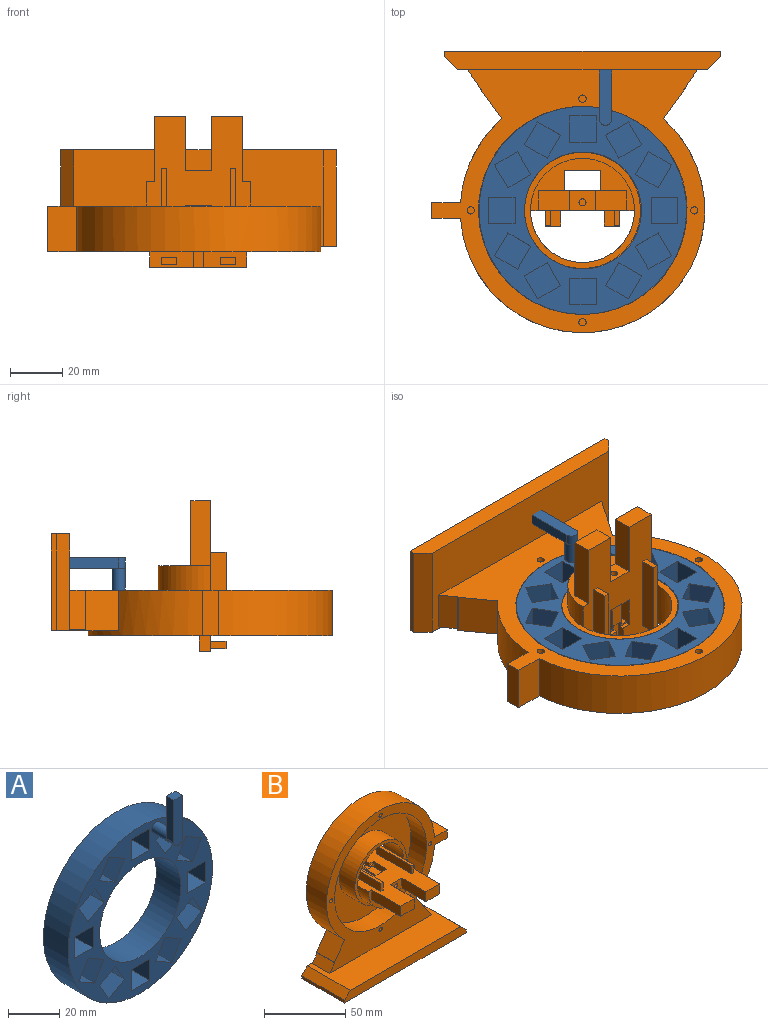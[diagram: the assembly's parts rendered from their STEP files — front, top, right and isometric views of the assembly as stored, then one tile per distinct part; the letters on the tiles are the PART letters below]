
ASSEMBLY  parts=2 mates=1
PART A: 72 faces, bbox 80x26x95.6 mm
  f0: plane 4.95x2.84mm, normal (0,-1,0), area 0.2mm2, adj f65,f67,f68,f70
  f1: plane 10.6x8.83mm, normal (-0.87,0,0.5), area 108.1mm2, adj f2,f38,f51,f64
  f2: plane 10.6x8.83mm, normal (0.5,0,0.87), area 108.1mm2, adj f1,f3,f51,f64
  f3: plane 10.6x8.83mm, normal (0.87,0,-0.5), area 108.1mm2, adj f2,f38,f51,f64
  f4: plane 10.6x8.83mm, normal (-0.87,0,-0.5), area 108.1mm2, adj f5,f39,f51,f63
  f5: plane 10.6x8.83mm, normal (-0.5,0,0.87), area 108.1mm2, adj f4,f6,f51,f63
  f6: plane 10.6x8.83mm, normal (0.87,0,0.5), area 108.1mm2, adj f5,f39,f51,f63
  f7: plane 10.6x10.2mm, normal (0,0,-1), area 108.1mm2, adj f8,f40,f51,f62
  f8: plane 10.6x10.2mm, normal (-1,0,0), area 108.1mm2, adj f7,f9,f51,f62
  f9: plane 10.6x10.2mm, normal (0,0,1), area 108.1mm2, adj f8,f40,f51,f62
  f10: plane 10.6x8.83mm, normal (0.87,0,-0.5), area 108.1mm2, adj f11,f41,f51,f61
  f11: plane 10.6x8.83mm, normal (-0.5,0,-0.87), area 108.1mm2, adj f10,f12,f51,f61
  f12: plane 10.6x8.83mm, normal (-0.87,0,0.5), area 108.1mm2, adj f11,f41,f51,f61
  f13: plane 10.6x8.83mm, normal (0.5,0,-0.87), area 108.1mm2, adj f14,f42,f51,f60
  f14: plane 10.6x8.83mm, normal (-0.87,0,-0.5), area 108.1mm2, adj f13,f15,f51,f60
  f15: plane 10.6x8.83mm, normal (-0.5,0,0.87), area 108.1mm2, adj f14,f42,f51,f60
  f16: plane 10.6x10.2mm, normal (1,0,0), area 108.1mm2, adj f17,f43,f51,f59
  f17: plane 10.6x10.2mm, normal (0,0,-1), area 108.1mm2, adj f16,f18,f51,f59
  f18: plane 10.6x10.2mm, normal (-1,0,0), area 108.1mm2, adj f17,f43,f51,f59
  f19: plane 10.6x8.83mm, normal (0.5,0,0.87), area 108.1mm2, adj f20,f44,f51,f58
  f20: plane 10.6x8.83mm, normal (0.87,0,-0.5), area 108.1mm2, adj f19,f21,f51,f58
  f21: plane 10.6x8.83mm, normal (-0.5,0,-0.87), area 108.1mm2, adj f20,f44,f51,f58
  f22: plane 10.6x8.83mm, normal (0.87,0,0.5), area 108.1mm2, adj f23,f45,f51,f57
  f23: plane 10.6x8.83mm, normal (0.5,0,-0.87), area 108.1mm2, adj f22,f24,f51,f57
  f24: plane 10.6x8.83mm, normal (-0.87,0,-0.5), area 108.1mm2, adj f23,f45,f51,f57
  f25: plane 10.6x10.2mm, normal (0,0,1), area 108.1mm2, adj f26,f46,f51,f56
  f26: plane 10.6x10.2mm, normal (1,0,0), area 108.1mm2, adj f25,f27,f51,f56
  f27: plane 10.6x10.2mm, normal (0,0,-1), area 108.1mm2, adj f26,f46,f51,f56
  f28: plane 10.6x8.83mm, normal (-0.87,0,0.5), area 108.1mm2, adj f29,f47,f51,f55
  f29: plane 10.6x8.83mm, normal (0.5,0,0.87), area 108.1mm2, adj f28,f30,f51,f55
  f30: plane 10.6x8.83mm, normal (0.87,0,-0.5), area 108.1mm2, adj f29,f47,f51,f55
  f31: plane 10.6x8.83mm, normal (-0.5,0,0.87), area 108.1mm2, adj f32,f48,f51,f54
  f32: plane 10.6x8.83mm, normal (0.87,0,0.5), area 108.1mm2, adj f31,f33,f51,f54
  f33: plane 10.6x8.83mm, normal (0.5,0,-0.87), area 108.1mm2, adj f32,f48,f51,f54
  f34: plane 10.6x10.2mm, normal (-1,0,0), area 108.1mm2, adj f35,f49,f51,f53
  f35: plane 10.6x10.2mm, normal (0,0,1), area 108.1mm2, adj f34,f36,f51,f53
  f36: plane 10.6x10.2mm, normal (1,0,0), area 108.1mm2, adj f35,f49,f51,f53
  f37: cylinder r=40mm len=80mm, axis (0,1,0), area 3418.1mm2, adj f51,f52
  f38: plane 10.6x8.83mm, normal (-0.5,0,-0.87), area 108.1mm2, adj f1,f3,f51,f64
  f39: plane 10.6x8.83mm, normal (0.5,0,-0.87), area 108.1mm2, adj f4,f6,f51,f63
  f40: plane 10.6x10.2mm, normal (1,0,0), area 108.1mm2, adj f7,f9,f51,f62
  f41: plane 10.6x8.83mm, normal (0.5,0,0.87), area 108.1mm2, adj f10,f12,f51,f61
  f42: plane 10.6x8.83mm, normal (0.87,0,0.5), area 108.1mm2, adj f13,f15,f51,f60
  f43: plane 10.6x10.2mm, normal (0,0,1), area 108.1mm2, adj f16,f18,f51,f59
  f44: plane 10.6x8.83mm, normal (-0.87,0,0.5), area 108.1mm2, adj f19,f21,f51,f58
  f45: plane 10.6x8.83mm, normal (-0.5,0,0.87), area 108.1mm2, adj f22,f24,f51,f57
  f46: plane 10.6x10.2mm, normal (-1,0,0), area 108.1mm2, adj f25,f27,f51,f56
  f47: plane 10.6x8.83mm, normal (-0.5,0,-0.87), area 108.1mm2, adj f28,f30,f51,f55
  f48: plane 10.6x8.83mm, normal (-0.87,0,-0.5), area 108.1mm2, adj f31,f33,f51,f54
  f49: plane 10.6x10.2mm, normal (0,0,-1), area 108.1mm2, adj f34,f36,f51,f53
  f50: cylinder r=22.5mm len=45mm, axis (0,1,0), area 1922.7mm2, adj f51,f52
  f51: plane 80x80mm, normal (0,-1,0), area 2168.4mm2, adj f1,f2,f3,f4,f5,f6,f7,f8
  f52: plane 80x80mm, normal (0,1,0), area 3436.1mm2, adj f37,f50
  f53: plane 10.2x10.2mm, normal (0,-1,0), area 104mm2, adj f34,f35,f36,f49
  f54: plane 13.93x13.93mm, normal (0,-1,0), area 104mm2, adj f31,f32,f33,f48
  f55: plane 13.93x13.93mm, normal (0,-1,0), area 104mm2, adj f28,f29,f30,f47
  f56: plane 10.2x10.2mm, normal (0,-1,0), area 104mm2, adj f25,f26,f27,f46
  f57: plane 13.93x13.93mm, normal (0,-1,0), area 104mm2, adj f22,f23,f24,f45
  f58: plane 13.93x13.93mm, normal (0,-1,0), area 104mm2, adj f19,f20,f21,f44
  f59: plane 10.2x10.2mm, normal (0,-1,0), area 104mm2, adj f16,f17,f18,f43
  f60: plane 13.93x13.93mm, normal (0,-1,0), area 104mm2, adj f13,f14,f15,f42
  f61: plane 13.93x13.93mm, normal (0,-1,0), area 104mm2, adj f10,f11,f12,f41
  f62: plane 10.2x10.2mm, normal (0,-1,0), area 104mm2, adj f7,f8,f9,f40
  f63: plane 13.93x13.93mm, normal (0,-1,0), area 104mm2, adj f4,f5,f6,f39
  f64: plane 13.93x13.93mm, normal (0,-1,0), area 104mm2, adj f1,f2,f3,f38
  f65: cylinder r=2.48mm len=8.3mm, axis (0,1,0), area 129.2mm2, adj f0,f51,f66
  f66: plane 19.94x4.9mm, normal (0,1,0), area 89.9mm2, adj f65,f68,f69,f70
  f67: cylinder r=2.45mm len=4.9mm, axis (0,1,0), area 31.6mm2, adj f0,f68,f70,f71
  f68: plane 20.3x4.1mm, normal (1,0,0), area 83.2mm2, adj f0,f66,f67,f69,f71
  f69: plane 4.9x4.1mm, normal (0,0,1), area 20.1mm2, adj f66,f68,f70,f71
  f70: plane 20.3x4.1mm, normal (-1,0,0), area 83.2mm2, adj f0,f66,f67,f69,f71
  f71: plane 22.75x4.9mm, normal (0,-1,0), area 108.9mm2, adj f67,f68,f69,f70
PART B: 124 faces, bbox 111x58x108.1 mm
  f0: plane 58x40mm, normal (0,0,1), area 1621.6mm2, adj f1,f2,f3,f4,f7,f8,f9,f19
  f1: plane 3.38x1.5mm, normal (0,-1,0), area 5.1mm2, adj f0,f9,f16,f101
  f2: plane 6x2mm, normal (0,1,0), area 12mm2, adj f0,f19,f46,f47
  f3: plane 6x2mm, normal (0,1,0), area 12mm2, adj f0,f43,f44,f45
  f4: plane 40x20mm, normal (0,1,0), area 303.4mm2, adj f0,f5,f17,f23,f24,f41,f42,f60
  f5: plane 19.01x5.3mm, normal (0,0,-1), area 52.7mm2, adj f4,f6,f20,f21,f22,f23,f40,f42
  f6: plane 4.7x1.3mm, normal (0,1,0), area 6.1mm2, adj f5,f20,f42,f61
  f7: plane 40x20mm, normal (0,-1,0), area 260.7mm2, adj f0,f41,f42,f49,f50,f51,f52,f92
  f8: plane 11.65x5.53mm, normal (1,0,0), area 57.8mm2, adj f0,f13,f14,f16,f90,f91,f93
  f9: plane 11.65x5.53mm, normal (-1,0,0), area 57.8mm2, adj f0,f1,f10,f12,f16,f91,f93
  f10: plane 4.03x2.5mm, normal (0,-1,0), area 10.1mm2, adj f9,f11,f16,f93
  f11: plane 10.03x4.03mm, normal (1,0,0), area 40.4mm2, adj f10,f12,f16,f93
  f12: plane 4.03x2.5mm, normal (0,1,0), area 10.1mm2, adj f9,f11,f16,f93
  f13: plane 4.03x2.5mm, normal (0,-1,0), area 10.1mm2, adj f8,f15,f16,f93
  f14: plane 4.03x2.5mm, normal (0,1,0), area 10.1mm2, adj f8,f15,f16,f93
  f15: plane 10.03x4.03mm, normal (-1,0,0), area 40.4mm2, adj f13,f14,f16,f93
  f16: plane 11.65x10.25mm, normal (0,0,1), area 62.3mm2, adj f1,f8,f9,f10,f11,f12,f13,f14
  f17: plane 19.01x5.22mm, normal (0,0,-1), area 51.2mm2, adj f4,f18,f24,f25,f26,f27,f28,f92
  f18: plane 7x4.7mm, normal (1,0,0), area 32.9mm2, adj f17,f25,f26,f60
  f19: plane 30.2x6mm, normal (-1,0,0), area 181.2mm2, adj f0,f2,f47,f59
  f20: plane 5.01x4.7mm, normal (-1,0,0), area 23.5mm2, adj f5,f6,f21,f61
  f21: plane 4.7x4mm, normal (0,1,0), area 18.8mm2, adj f5,f20,f40,f61
  f22: plane 4.7x4mm, normal (0,-1,0), area 18.8mm2, adj f5,f23,f40,f61
  f23: plane 7x4.7mm, normal (-1,0,0), area 32.9mm2, adj f4,f5,f22,f61
  f24: plane 7x4.7mm, normal (1,0,0), area 32.9mm2, adj f4,f17,f25,f60
  f25: plane 4.7x4mm, normal (0,-1,0), area 18.8mm2, adj f17,f18,f24,f60
  f26: plane 4.7x4mm, normal (0,1,0), area 18.8mm2, adj f17,f18,f27,f60
  f27: plane 5.01x4.7mm, normal (1,0,0), area 23.5mm2, adj f17,f26,f28,f60
  f28: plane 4.7x1.22mm, normal (0,1,0), area 5.7mm2, adj f17,f27,f60,f92
  f29: plane 106x37.2mm, normal (0,0,-1), area 3778.4mm2, adj f31,f73,f74,f77,f79,f80,f81
  f30: plane 105x101.14mm, normal (0,-1,0), area 2880mm2, adj f32,f33,f36,f37,f68,f69,f70,f71
  f31: plane 106x25.92mm, normal (0,1,0), area 1453.7mm2, adj f29,f36,f37,f69,f70,f71,f72,f73
  f32: plane 15x6.12mm, normal (-0.82,0,0.57), area 111.8mm2, adj f30,f34,f36,f72
  f33: plane 15x6.12mm, normal (0.82,0,0.57), area 111.8mm2, adj f30,f35,f37,f72
  f34: plane 13.03x6.12mm, normal (0,1,0), area 38.2mm2, adj f32,f36,f72
  f35: plane 13.03x6.12mm, normal (0,1,0), area 38.2mm2, adj f33,f37,f72
  f36: cylinder r=62.5mm len=15.6mm, axis (0,1,0), area 9.5mm2, adj f30,f31,f32,f34,f70,f72
  f37: cylinder r=62.5mm len=15.6mm, axis (0,1,0), area 9.6mm2, adj f30,f31,f33,f35,f69,f72
  f38: plane 80x80mm, normal (0,-1,0), area 3460.8mm2, adj f67,f68
  f39: plane 44.65x44.65mm, normal (0,-1,0), area 309.2mm2, adj f50,f66,f67
  f40: plane 7x4.7mm, normal (-1,0,0), area 32.9mm2, adj f5,f21,f22,f61
  f41: plane 25x14.08mm, normal (0,0,1), area 352mm2, adj f4,f7,f42,f92
  f42: plane 25x9.97mm, normal (-1,0,0), area 160mm2, adj f4,f5,f6,f7,f41,f61,f93,f94
  f43: plane 30.2x6mm, normal (-1,0,0), area 181.2mm2, adj f0,f3,f45,f58
  f44: plane 30.2x6mm, normal (1,0,0), area 181.2mm2, adj f0,f3,f45,f58
  f45: plane 30.2x2mm, normal (0,0,1), area 60.4mm2, adj f3,f43,f44,f58
  f46: plane 30.2x6mm, normal (1,0,0), area 181.2mm2, adj f0,f2,f47,f59
  f47: plane 30.2x2mm, normal (0,0,1), area 60.4mm2, adj f2,f19,f46,f59
  f48: plane 12x7.5mm, normal (0,-1,0), area 90mm2, adj f0,f49,f51,f54
  f49: plane 34x25mm, normal (0,0,-1), area 642mm2, adj f7,f48,f51,f52,f53,f54,f55,f56
  f50: cylinder r=20mm len=40mm, axis (0,1,0), area 590.6mm2, adj f0,f7,f39
  f51: plane 25x7.5mm, normal (-1,0,0), area 187.5mm2, adj f0,f7,f48,f49
  f52: plane 25x7.5mm, normal (1,0,0), area 187.5mm2, adj f0,f7,f49,f53
  f53: plane 12x7.5mm, normal (0,-1,0), area 90mm2, adj f0,f49,f52,f55
  f54: plane 20.8x7.5mm, normal (1,0,0), area 156mm2, adj f0,f48,f49,f56
  f55: plane 20.8x7.5mm, normal (-1,0,0), area 156mm2, adj f0,f49,f53,f56
  f56: plane 10x7.5mm, normal (0,-1,0), area 69.3mm2, adj f0,f49,f54,f55,f57
  f57: cylinder r=1.35mm len=6.19mm, axis (0,1,0), area 52.5mm2, adj f56,f82
  f58: plane 6x2mm, normal (0,-1,0), area 12mm2, adj f0,f43,f44,f45
  f59: plane 6x2mm, normal (0,-1,0), area 12mm2, adj f0,f19,f46,f47
  f60: plane 19.01x5.22mm, normal (0,0,1), area 51.2mm2, adj f4,f18,f24,f25,f26,f27,f28,f92
  f61: plane 19.01x5.3mm, normal (0,0,1), area 52.7mm2, adj f4,f6,f20,f21,f22,f23,f40,f42
  f62: cylinder r=1.4mm len=15.1mm, axis (0,1,0), area 86.4mm2, adj f4,f63,f83,f84,f85
  f63: plane 2.8x2.8mm, normal (0,1,0), area 6.2mm2, adj f62
  f64: cylinder r=1.4mm len=15.1mm, axis (0,1,0), area 86.4mm2, adj f4,f65,f86,f87,f88
  f65: plane 2.8x2.8mm, normal (0,1,0), area 6.2mm2, adj f64
  f66: cylinder r=20mm len=40mm, axis (0,-1,0), area 1231.5mm2, adj f0,f4,f39,f89
  f67: cylinder r=22.33mm len=44.65mm, axis (0,-1,0), area 1907.7mm2, adj f38,f39
  f68: cylinder r=40mm len=80mm, axis (0,-1,0), area 3418.1mm2, adj f30,f38
  f69: plane 15.6x12.55mm, normal (0.81,0,0.59), area 242.5mm2, adj f30,f31,f37,f71
  f70: plane 15.6x12.67mm, normal (-0.81,0,0.58), area 242.8mm2, adj f30,f31,f36,f71
  f71: cylinder r=47mm len=94mm, axis (0,-1,0), area 4033.4mm2, adj f30,f31,f69,f70,f89,f122,f123
  f72: plane 96x37.2mm, normal (0,0,1), area 2206mm2, adj f30,f31,f32,f33,f34,f35,f36,f37
  f73: plane 37.2x2mm, normal (-1,0,0), area 74.4mm2, adj f29,f31,f75,f77
  f74: plane 37.2x2mm, normal (1,0,0), area 74.4mm2, adj f29,f31,f76,f77
  f75: plane 37.2x5mm, normal (-0.71,0,0.71), area 263mm2, adj f31,f72,f73,f77
  f76: plane 37.2x5mm, normal (0.71,0,0.71), area 263mm2, adj f31,f72,f74,f77
  f77: plane 106x7mm, normal (0,-1,0), area 717mm2, adj f29,f72,f73,f74,f75,f76
  f78: plane 16x10.3mm, normal (0,0,-1), area 164.8mm2, adj f31,f79,f80,f81
  f79: plane 10.3x7mm, normal (-1,0,0), area 72.1mm2, adj f29,f31,f78,f81
  f80: plane 10.3x7mm, normal (1,0,0), area 72.1mm2, adj f29,f31,f78,f81
  f81: plane 16x7mm, normal (0,1,0), area 112mm2, adj f29,f78,f79,f80
  f82: plane 2.7x2.7mm, normal (0,-1,0), area 5.7mm2, adj f57
  f83: plane 2.8x2.4mm, normal (0,1,0), area 5.6mm2, adj f62,f85
  f84: plane 2.8x2.4mm, normal (0,-1,0), area 5.6mm2, adj f62,f85
  f85: plane 7x1.96mm, normal (-1,0,0), area 13.7mm2, adj f62,f83,f84
  f86: plane 2.8x2.4mm, normal (0,1,0), area 5.6mm2, adj f64,f88
  f87: plane 2.8x2.4mm, normal (0,-1,0), area 5.6mm2, adj f64,f88
  f88: plane 7x1.96mm, normal (1,0,0), area 13.7mm2, adj f64,f86,f87
  f89: plane 105x94mm, normal (0,1,0), area 5749.3mm2, adj f66,f71,f121,f122,f123
  f90: plane 3.38x1.5mm, normal (0,-1,0), area 5.1mm2, adj f0,f8,f16,f99
  f91: plane 10.25x1.5mm, normal (0,1,0), area 15.4mm2, adj f0,f8,f9,f16
  f92: plane 25x9.97mm, normal (1,0,0), area 160mm2, adj f4,f7,f17,f28,f41,f60,f93,f94
  f93: plane 25x14.08mm, normal (0,0,-1), area 301.8mm2, adj f4,f8,f9,f10,f11,f12,f13,f14
  f94: plane 14.08x1.97mm, normal (0,1,0), area 27.8mm2, adj f42,f49,f92,f93
  f95: plane 8x4.3mm, normal (1,0,0), area 34.4mm2, adj f0,f4,f96,f98
  f96: plane 37.31x8mm, normal (0,0,-1), area 298.5mm2, adj f4,f95,f97,f98
  f97: plane 8x4.3mm, normal (-1,0,0), area 34.4mm2, adj f0,f4,f96,f98
  f98: plane 37.31x4.3mm, normal (0,1,0), area 152.3mm2, adj f0,f95,f96,f97,f99,f101,f102
  f99: plane 14.18x2.3mm, normal (1,0,0), area 29.6mm2, adj f0,f16,f90,f98,f100,f102
  f100: plane 3.5x0.8mm, normal (0,1,0), area 2.8mm2, adj f16,f99,f101,f102
  f101: plane 14.18x2.3mm, normal (-1,0,0), area 29.6mm2, adj f0,f1,f16,f98,f100,f102
  f102: plane 14.18x3.5mm, normal (0,0,1), area 49.6mm2, adj f98,f99,f100,f101
  f103: plane 6x6mm, normal (0,1,0), area 36mm2, adj f0,f104,f106,f107
  f104: plane 6x3mm, normal (-1,0,0), area 18mm2, adj f0,f103,f105,f107
  f105: plane 6x6mm, normal (0,-1,0), area 36mm2, adj f0,f104,f106,f107
  f106: plane 6x3mm, normal (1,0,0), area 18mm2, adj f0,f103,f105,f107
  f107: plane 6x3mm, normal (0,0,1), area 18mm2, adj f103,f104,f105,f106
  f108: plane 6x6mm, normal (0,1,0), area 36mm2, adj f0,f109,f111,f112
  f109: plane 6x3mm, normal (-1,0,0), area 18mm2, adj f0,f108,f110,f112
  f110: plane 6x6mm, normal (0,-1,0), area 36mm2, adj f0,f109,f111,f112
  f111: plane 6x3mm, normal (1,0,0), area 18mm2, adj f0,f108,f110,f112
  f112: plane 6x3mm, normal (0,0,1), area 18mm2, adj f108,f109,f110,f111
  f113: cylinder r=1.4mm len=15mm, axis (0,-1,0), area 131.9mm2, adj f30,f114
  f114: plane 2.8x2.8mm, normal (0,-1,0), area 6.2mm2, adj f113
  f115: cylinder r=1.4mm len=15mm, axis (0,-1,0), area 131.9mm2, adj f30,f116
  f116: plane 2.8x2.8mm, normal (0,-1,0), area 6.2mm2, adj f115
  f117: cylinder r=1.4mm len=15mm, axis (0,-1,0), area 131.9mm2, adj f30,f118
  f118: plane 2.8x2.8mm, normal (0,-1,0), area 6.2mm2, adj f117
  f119: cylinder r=1.4mm len=15mm, axis (0,-1,0), area 131.9mm2, adj f30,f120
  f120: plane 2.8x2.8mm, normal (0,-1,0), area 6.2mm2, adj f119
  f121: plane 17.6x6mm, normal (1,0,0), area 105.6mm2, adj f30,f89,f122,f123
  f122: plane 17.6x11.1mm, normal (0,0,1), area 195.3mm2, adj f30,f71,f89,f121
  f123: plane 17.6x11.1mm, normal (0,0,-1), area 195.3mm2, adj f30,f71,f89,f121
PLACE A rot(axis=(-1,0,0),90deg) t=(-12.16,162.09,63.4)mm
PLACE B rot(axis=(0,-0.71,0.71),180deg) t=(-12.37,162.09,63.4)mm fixed
MATE planar B.f68 <-> A.f37  axis (0,0,1) through (-12.37,162.09,60.4)mm
